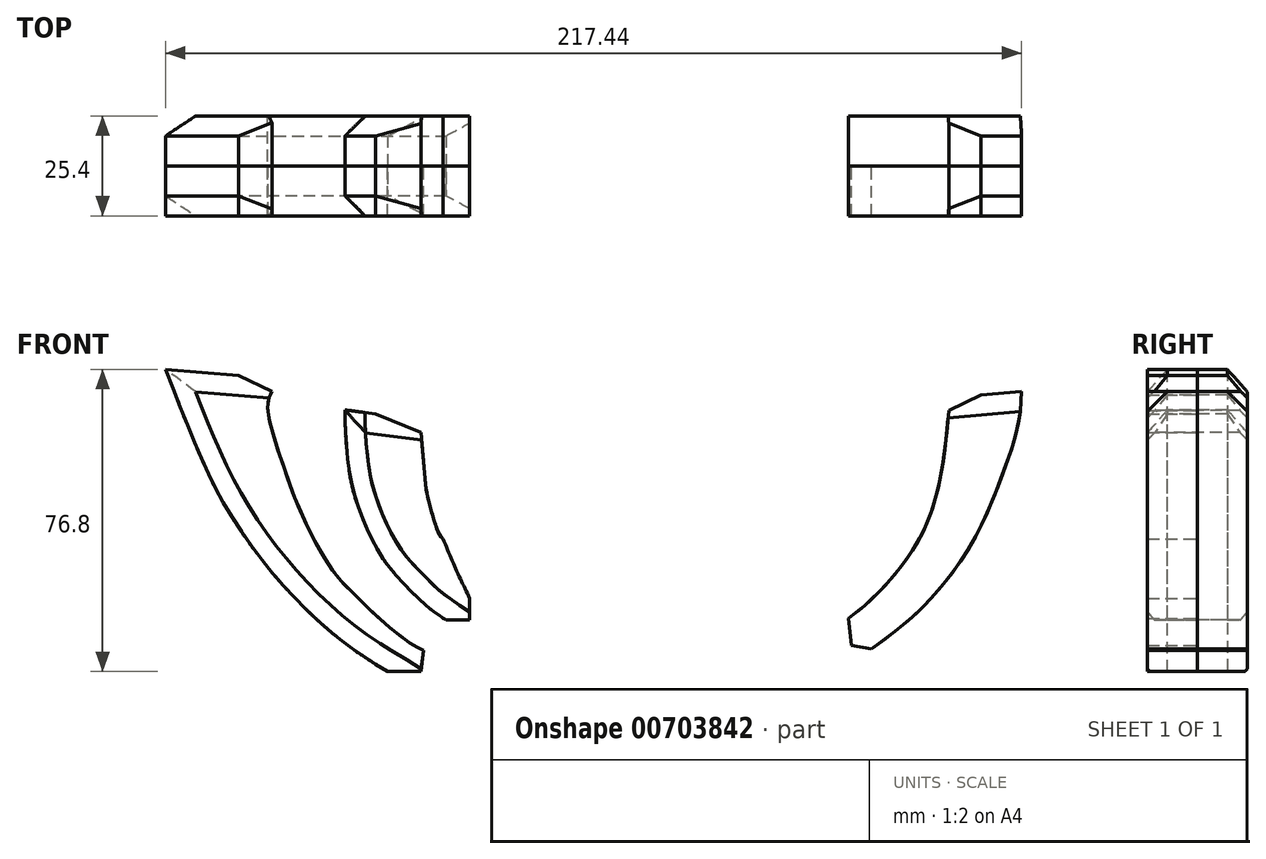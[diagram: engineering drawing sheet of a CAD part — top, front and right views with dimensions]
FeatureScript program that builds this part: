
annotation { "Feature Type Name" : "Feature", "Feature Type Description" : "" }
export const myFeature = defineFeature(function(context is Context, id is Id, definition is map)
    precondition{}
    {
        {
            var Q0;
            Q0=qCreatedBy(makeId("Front.planeOp"),FACE);
            var sketch = newSketch(context, id + "F0", { "sketchPlane" : qUnion([Q0])});
            skLineSegment(sketch, "E0", {"start": v(-122.31, 49.69) * mm, "end": v(-103.8, 48.16) * mm});
            skLineSegment(sketch, "E1", {"start": v(-103.8, 48.16) * mm, "end": v(-95.32, 44.06) * mm});
            skLineSegment(sketch, "E2", {"start": v(-95.32, 44.06) * mm, "end": v(-85.2, 43.1) * mm});
            skLineSegment(sketch, "E3", {"start": v(-85.2, 43.1) * mm, "end": v(-76.71, 39.38) * mm});
            skLineSegment(sketch, "E4", {"start": v(-76.71, 39.38) * mm, "end": v(-68.96, 38.36) * mm});
            skLineSegment(sketch, "E5", {"start": v(-68.96, 38.36) * mm, "end": v(-57.43, 33.63) * mm});
            skFitSpline(sketch, "E6", {"points": [v(-57.43, 33.63) * mm, v(-56.85, 26.65) * mm, v(-56.16, 19.73) * mm, v(-55.33, 15.7) * mm, v(-54.2, 11.73) * mm, v(-52.95, 8.15) * mm, v(-51.8, 6.64) * mm], "startDerivative": vector(2.75, -32.82) * mm, "endDerivative": vector(10.96, -11.97) * mm});
            skFitSpline(sketch, "E7", {"points": [v(-122.31, 49.69) * mm, v(-114.04, 28.95) * mm, v(-106.9, 14.55) * mm, v(-96.83, 0) * mm, v(-86.28, -11.6) * mm, v(-75.84, -20.58) * mm, v(-65.88, -27.11) * mm], "startDerivative": vector(42.95, -111.11) * mm, "endDerivative": vector(69.64, -42.92) * mm});
            skLineSegment(sketch, "E8", {"start": v(-65.88, -27.11) * mm, "end": v(-57.47, -27.11) * mm});
            skLineSegment(sketch, "E9", {"start": v(-57.47, -27.11) * mm, "end": v(-56.75, -21.74) * mm});
            skLineSegment(sketch, "E10", {"start": v(-56.75, -21.74) * mm, "end": v(-51.68, -19.86) * mm});
            skLineSegment(sketch, "E11", {"start": v(-51.68, -19.86) * mm, "end": v(-51.05, -14.03) * mm});
            skLineSegment(sketch, "E12", {"start": v(-51.05, -14.03) * mm, "end": v(-45.06, -14.03) * mm});
            skLineSegment(sketch, "E13", {"start": v(-45.06, -14.03) * mm, "end": v(-45.06, -8.46) * mm});
            skLineSegment(sketch, "E14", {"start": v(122.2, 49.63) * mm, "end": v(104, 48.25) * mm});
            skLineSegment(sketch, "E15", {"start": v(104, 48.25) * mm, "end": v(95.13, 44.09) * mm});
            skLineSegment(sketch, "E16", {"start": v(95.13, 44.09) * mm, "end": v(84.88, 43.17) * mm});
            skLineSegment(sketch, "E17", {"start": v(84.88, 43.17) * mm, "end": v(76.66, 39.2) * mm});
            skLineSegment(sketch, "E18", {"start": v(76.66, 39.2) * mm, "end": v(69.2, 38.51) * mm});
            skLineSegment(sketch, "E19", {"start": v(69.2, 38.51) * mm, "end": v(56.96, 33.46) * mm});
            skFitSpline(sketch, "E20", {"points": [v(56.96, 33.46) * mm, v(56.22, 21.38) * mm, v(54.75, 14.45) * mm, v(52.8, 8.08) * mm, v(51.9, 6.62) * mm], "startDerivative": vector(-1.32, -37.72) * mm, "endDerivative": vector(-6.66, -8.71) * mm});
            skFitSpline(sketch, "E21", {"points": [v(122.2, 49.63) * mm, v(115.67, 32.4) * mm, v(107.79, 15.56) * mm, v(101.55, 5.56) * mm, v(95.31, -2.56) * mm, v(87.2, -11.03) * mm, v(79.66, -17.74) * mm, v(71.9, -23.74) * mm, v(65.9, -27.08) * mm], "startDerivative": vector(-39.57, -109.68) * mm, "endDerivative": vector(-61.7, -30.96) * mm});
            skLineSegment(sketch, "E22", {"start": v(65.9, -27.08) * mm, "end": v(57.32, -27.48) * mm});
            skLineSegment(sketch, "E23", {"start": v(57.32, -27.48) * mm, "end": v(57.03, -21.4) * mm});
            skLineSegment(sketch, "E24", {"start": v(57.03, -21.4) * mm, "end": v(51.88, -20.45) * mm});
            skLineSegment(sketch, "E25", {"start": v(51.88, -20.45) * mm, "end": v(51.12, -13.55) * mm});
            skLineSegment(sketch, "E26", {"start": v(51.12, -13.55) * mm, "end": v(44.82, -14.1) * mm});
            skLineSegment(sketch, "E27", {"start": v(44.82, -14.1) * mm, "end": v(45.4, -7.48) * mm});
            skFitSpline(sketch, "E28", {"points": [v(-51.8, 6.64) * mm, v(-48.35, -1.52) * mm, v(-45.06, -8.46) * mm], "startDerivative": vector(6.64, -16.1) * mm, "endDerivative": vector(6.86, -14.06) * mm});
            skFitSpline(sketch, "E29", {"points": [v(51.9, 6.62) * mm, v(49.56, 0) * mm, v(45.4, -7.48) * mm], "startDerivative": vector(-4.2, -13.85) * mm, "endDerivative": vector(-8.72, -14.35) * mm});
            skSolve(sketch);
        }
        {
            var Q0;
            Q0=makeQuery(id+"F0.imprint","IMPRINT",FACE,{"disambiguationData":[TD([[makeQuery(id+"F0.imprint","IMPRINT",EDGE,{"derivedFrom":sQuery(id+"F0.wireOp",EDGE,"E0")}),-1.0]])]});
            var Q1;
            Q1=makeQuery(id+"F0.imprint","IMPRINT",FACE,{"disambiguationData":[TD([[makeQuery(id+"F0.imprint","IMPRINT",EDGE,{"derivedFrom":sQuery(id+"F0.wireOp",EDGE,"E14")}),1.0]])]});
            extrude(context, id + "F1", {"entities" : qUnion([Q0, Q1]), "depth" : 12.7 * mm, "offsetDistance" : 25.4 * mm});
        }
        {
            var Q0;
            Q0=makeQuery(id+"F1.opExtrude","CAP_FACE",FACE,{"disambiguationData":[OSD([sQuery(id+"F0.wireOp",EDGE,"E0"),sQuery(id+"F0.wireOp",EDGE,"E1"),sQuery(id+"F0.wireOp",EDGE,"E2"),sQuery(id+"F0.wireOp",EDGE,"E3"),sQuery(id+"F0.wireOp",EDGE,"E4"),sQuery(id+"F0.wireOp",EDGE,"E5"),sQuery(id+"F0.wireOp",EDGE,"E6"),sQuery(id+"F0.wireOp",EDGE,"E7"),sQuery(id+"F0.wireOp",EDGE,"E8"),sQuery(id+"F0.wireOp",EDGE,"E9"),sQuery(id+"F0.wireOp",EDGE,"E10"),sQuery(id+"F0.wireOp",EDGE,"E11"),sQuery(id+"F0.wireOp",EDGE,"E12"),sQuery(id+"F0.wireOp",EDGE,"E13"),sQuery(id+"F0.wireOp",EDGE,"E28")])],"isStart":false});
            var Q1;
            Q1=makeQuery(id+"F1.opExtrude","CAP_FACE",FACE,{"disambiguationData":[OSD([sQuery(id+"F0.wireOp",EDGE,"E14"),sQuery(id+"F0.wireOp",EDGE,"E15"),sQuery(id+"F0.wireOp",EDGE,"E16"),sQuery(id+"F0.wireOp",EDGE,"E17"),sQuery(id+"F0.wireOp",EDGE,"E18"),sQuery(id+"F0.wireOp",EDGE,"E19"),sQuery(id+"F0.wireOp",EDGE,"E20"),sQuery(id+"F0.wireOp",EDGE,"E21"),sQuery(id+"F0.wireOp",EDGE,"E22"),sQuery(id+"F0.wireOp",EDGE,"E23"),sQuery(id+"F0.wireOp",EDGE,"E24"),sQuery(id+"F0.wireOp",EDGE,"E25"),sQuery(id+"F0.wireOp",EDGE,"E26"),sQuery(id+"F0.wireOp",EDGE,"E27"),sQuery(id+"F0.wireOp",EDGE,"E29")])],"isStart":false});
            extrude(context, id + "F2", {"entities" : qUnion([Q0, Q1]), "oppositeDirection" : true, "depth" : 25.4 * mm, "offsetDistance" : 25.4 * mm});
        }
        {
            var Q0;
            Q0=makeQuery(id+"F2.opExtrude","CAP_FACE",FACE,{"disambiguationData":[OSD([sQuery(id+"F0.wireOp",EDGE,"E14"),sQuery(id+"F0.wireOp",EDGE,"E15"),sQuery(id+"F0.wireOp",EDGE,"E16"),sQuery(id+"F0.wireOp",EDGE,"E17"),sQuery(id+"F0.wireOp",EDGE,"E18"),sQuery(id+"F0.wireOp",EDGE,"E19"),sQuery(id+"F0.wireOp",EDGE,"E20"),sQuery(id+"F0.wireOp",EDGE,"E21"),sQuery(id+"F0.wireOp",EDGE,"E22"),sQuery(id+"F0.wireOp",EDGE,"E23"),sQuery(id+"F0.wireOp",EDGE,"E24"),sQuery(id+"F0.wireOp",EDGE,"E25"),sQuery(id+"F0.wireOp",EDGE,"E26"),sQuery(id+"F0.wireOp",EDGE,"E27"),sQuery(id+"F0.wireOp",EDGE,"E29")])],"isStart":false});
            var sketch = newSketch(context, id + "F3", { "sketchPlane" : qUnion([Q0])});
            skFitSpline(sketch, "E30", {"points": [v(-76.66, 39.2) * mm, v(-75.08, 25.26) * mm, v(-71.57, 11.76) * mm, v(-64.87, 0) * mm, v(-55.73, -9.93) * mm, v(-51.12, -13.55) * mm], "startDerivative": vector(5.7, -64.2) * mm, "endDerivative": vector(30.19, -21.67) * mm});
            skFitSpline(sketch, "E31", {"points": [v(-95.13, 44.09) * mm, v(-94.28, 35.68) * mm, v(-89, 19.48) * mm, v(-81.68, 4.14) * mm, v(-70.92, -9.87) * mm, v(-62.77, -17.08) * mm, v(-57.03, -21.4) * mm], "startDerivative": vector(1.9, -56.55) * mm, "endDerivative": vector(44.32, -32.83) * mm});
            skSolve(sketch);
        }
        {
            var Q0;
            Q0=makeQuery(id+"F2.opExtrude","CAP_FACE",FACE,{"disambiguationData":[OSD([sQuery(id+"F0.wireOp",EDGE,"E0"),sQuery(id+"F0.wireOp",EDGE,"E1"),sQuery(id+"F0.wireOp",EDGE,"E2"),sQuery(id+"F0.wireOp",EDGE,"E3"),sQuery(id+"F0.wireOp",EDGE,"E4"),sQuery(id+"F0.wireOp",EDGE,"E5"),sQuery(id+"F0.wireOp",EDGE,"E6"),sQuery(id+"F0.wireOp",EDGE,"E7"),sQuery(id+"F0.wireOp",EDGE,"E8"),sQuery(id+"F0.wireOp",EDGE,"E9"),sQuery(id+"F0.wireOp",EDGE,"E10"),sQuery(id+"F0.wireOp",EDGE,"E11"),sQuery(id+"F0.wireOp",EDGE,"E12"),sQuery(id+"F0.wireOp",EDGE,"E13"),sQuery(id+"F0.wireOp",EDGE,"E28")])],"isStart":false});
            var sketch = newSketch(context, id + "F4", { "sketchPlane" : qUnion([Q0])});
            skFitSpline(sketch, "E32", {"points": [v(95.32, 44.06) * mm, v(96.37, 40.15) * mm, v(93, 26.9) * mm, v(88.3, 14.26) * mm, v(80.83, 0) * mm, v(74.33, -7.54) * mm, v(66.38, -15) * mm, v(59.64, -20.18) * mm, v(56.75, -21.74) * mm], "startDerivative": vector(19.35, -39.65) * mm, "endDerivative": vector(-35.72, -17.16) * mm});
            skFitSpline(sketch, "E33", {"points": [v(76.71, 39.38) * mm, v(76.71, 37.02) * mm, v(75.69, 24.01) * mm, v(72.57, 12.56) * mm, v(67.74, 2.63) * mm, v(61.87, -4.66) * mm, v(55.16, -11.1) * mm, v(51.05, -14.03) * mm], "startDerivative": vector(0.5, -24.06) * mm, "endDerivative": vector(-35.03, -22.95) * mm});
            skSolve(sketch);
        }
        {
            var Q0;
            Q0=makeQuery(id+"F4.imprint","IMPRINT",FACE,{"disambiguationData":[TD([[makeQuery(id+"F4.imprint","IMPRINT",EDGE,{"derivedFrom":sQuery(id+"F4.wireOp",EDGE,"E32")}),-1.0]])]});
            extrude(context, id + "F5", {"entities" : qUnion([Q0]), "operationType" : NewBodyOperationType.REMOVE, "oppositeDirection" : true, "depth" : 25.4 * mm, "offsetDistance" : 25.4 * mm});
        }
        {
            var Q0;
            Q0=makeQuery(id+"F3.imprint","IMPRINT",FACE,{"disambiguationData":[TD([[makeQuery(id+"F3.imprint","IMPRINT",EDGE,{"derivedFrom":sQuery(id+"F3.wireOp",EDGE,"E30")}),1.0]])]});
            var Q1;
            Q1=makeQuery(id+"F3.imprint","IMPRINT",FACE,{"disambiguationData":[TD([[makeQuery(id+"F3.imprint","IMPRINT",EDGE,{"derivedFrom":sQuery(id+"F3.wireOp",EDGE,"E31")}),-1.0]])]});
            extrude(context, id + "F6", {"entities" : qUnion([Q0, Q1]), "operationType" : NewBodyOperationType.REMOVE, "oppositeDirection" : true, "depth" : 25.4 * mm, "offsetDistance" : 25.4 * mm});
        }
        {
            var Q0;
            Q0=makeQuery(id+"F6.boolean.opBoolean","COPY",EDGE,{"derivedFrom":makeQuery(id+"F6.opExtrude","CAP_EDGE",EDGE,{"disambiguationData":[OSD([sQuery(id+"F3.wireOp",EDGE,"E31")])],"isStart":true})});
            var Q1;
            Q1=makeQuery(id+"F2.opExtrude","CAP_EDGE",EDGE,{"disambiguationData":[OSD([sQuery(id+"F0.wireOp",EDGE,"E16")])],"isStart":false});
            chamfer(context, id + "F7", {"entities" : qUnion([Q0, Q1]), "width" : 5.08 * mm, "tangentPropagation" : true});
        }
        {
            var Q0;
            Q0=makeQuery(id+"F2.opExtrude","CAP_EDGE",EDGE,{"disambiguationData":[OSD([sQuery(id+"F0.wireOp",EDGE,"E7")])],"isStart":false});
            var Q1;
            Q1=makeQuery(id+"F2.opExtrude","CAP_EDGE",EDGE,{"disambiguationData":[OSD([sQuery(id+"F0.wireOp",EDGE,"E0")])],"isStart":false});
            chamfer(context, id + "F8", {"entities" : qUnion([Q0, Q1]), "width" : 5.08 * mm, "tangentPropagation" : true});
        }
        {
            var Q0;
            Q0=makeQuery(id+"F5.boolean.opBoolean","COPY",EDGE,{"derivedFrom":makeQuery(id+"F5.opExtrude","CAP_EDGE",EDGE,{"disambiguationData":[OSD([sQuery(id+"F4.wireOp",EDGE,"E33")])],"isStart":true})});
            var Q1;
            Q1=makeQuery(id+"F2.opExtrude","CAP_EDGE",EDGE,{"disambiguationData":[OSD([sQuery(id+"F0.wireOp",EDGE,"E4")])],"isStart":false});
            chamfer(context, id + "F9", {"entities" : qUnion([Q0, Q1]), "width" : 5.08 * mm, "tangentPropagation" : true});
        }
        {
            var Q0;
            Q0=makeQuery(id+"F6.boolean.opBoolean","COPY",EDGE,{"derivedFrom":makeQuery(id+"F6.opExtrude","CAP_EDGE",EDGE,{"disambiguationData":[OSD([sQuery(id+"F3.wireOp",EDGE,"E31")])],"isStart":false})});
            var Q1;
            Q1=makeQuery(id+"F2.opExtrude","CAP_EDGE",EDGE,{"disambiguationData":[OSD([sQuery(id+"F0.wireOp",EDGE,"E16")])],"isStart":true});
            var Q2;
            Q2=makeQuery(id+"F2.opExtrude","CAP_EDGE",EDGE,{"disambiguationData":[OSD([sQuery(id+"F0.wireOp",EDGE,"E7")])],"isStart":true});
            var Q3;
            Q3=makeQuery(id+"F2.opExtrude","CAP_EDGE",EDGE,{"disambiguationData":[OSD([sQuery(id+"F0.wireOp",EDGE,"E0")])],"isStart":true});
            var Q4;
            Q4=makeQuery(id+"F2.opExtrude","CAP_EDGE",EDGE,{"disambiguationData":[OSD([sQuery(id+"F0.wireOp",EDGE,"E4")])],"isStart":true});
            var Q5;
            Q5=makeQuery(id+"F5.boolean.opBoolean","COPY",EDGE,{"derivedFrom":makeQuery(id+"F5.opExtrude","CAP_EDGE",EDGE,{"disambiguationData":[OSD([sQuery(id+"F4.wireOp",EDGE,"E33")])],"isStart":false})});
            chamfer(context, id + "F10", {"entities" : qUnion([Q0, Q1, Q2, Q3, Q4, Q5]), "width" : 5.08 * mm, "tangentPropagation" : true});
        }
    });
